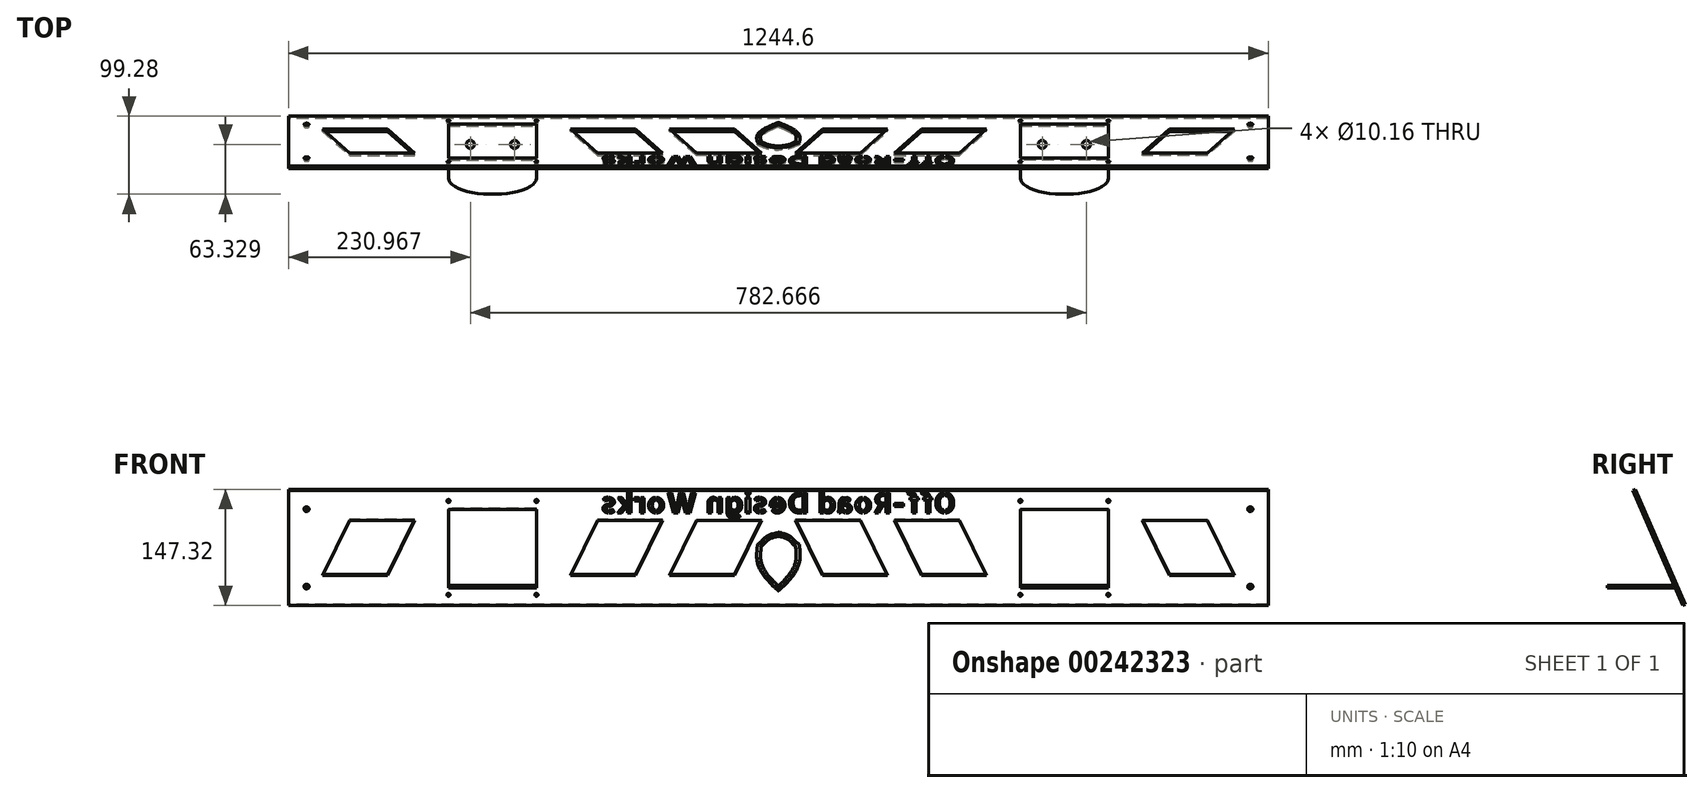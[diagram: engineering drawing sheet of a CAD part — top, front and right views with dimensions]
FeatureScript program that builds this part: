
annotation { "Feature Type Name" : "Feature", "Feature Type Description" : "" }
export const myFeature = defineFeature(function(context is Context, id is Id, definition is map)
    precondition{}
    {
        {
            var Q0;
            Q0=qCreatedBy(makeId("Right.planeOp"),FACE);
            var sketch = newSketch(context, id + "F0", { "sketchPlane" : qUnion([Q0])});
            skLineSegment(sketch, "E0", {"start": v(0, 0) * mm, "end": v(-63.5, 146.05) * mm});
            skLineSegment(sketch, "E1", {"start": v(-63.5, 146.05) * mm, "end": v(-66.41, 144.78) * mm});
            skLineSegment(sketch, "E2", {"start": v(-66.41, 144.78) * mm, "end": v(-2.91, -1.27) * mm});
            skLineSegment(sketch, "E3", {"start": v(-2.91, -1.27) * mm, "end": v(0, 0) * mm});
            skSolve(sketch);
        }
        {
            var Q0;
            Q0 = qSketchRegion(id + "F0", true);
            extrude(context, id + "F1", {"entities" : qUnion([Q0]), "depth" : 622.3 * mm, "hasSecondDirection" : true, "secondDirectionOppositeDirection" : true, "secondDirectionDepth" : 622.3 * mm});
        }
        {
            var Q0;
            Q0=makeQuery(id+"F1.opExtrude","SWEPT_FACE",FACE,{"disambiguationData":[OSD([sQuery(id+"F0.wireOp",EDGE,"E0")])]});
            var sketch = newSketch(context, id + "F2", { "sketchPlane" : qUnion([Q0])});
            skSolve(sketch);
        }
        {
            var Q0;
            {var subQ0=sQuery(id+"F0.wireOp",EDGE,"E0");Q0=makeQuery(id+"F2.imprint","IMPRINT",FACE,{"disambiguationData":[TD([[makeQuery(id+"F2.imprint","IMPRINT",EDGE,{"derivedFrom":makeQuery(id+"F1.opExtrude","CAP_EDGE",EDGE,{"disambiguationData":[OSD([subQ0])],"isStart":true})}),1.0]])]});}
            var sketch = newSketch(context, id + "F3", { "sketchPlane" : qUnion([Q0])});
            skLineSegment(sketch, "E4", {"start": v(0, 0) * mm, "end": v(0, -192.6) * mm, "construction": true});
            skLineSegment(sketch, "E5", {"start": v(-307.34, 133.22) * mm, "end": v(-419.1, 133.22) * mm});
            skLineSegment(sketch, "E6", {"start": v(-419.1, 133.22) * mm, "end": v(-419.1, 26.03) * mm});
            skLineSegment(sketch, "E7", {"start": v(-419.1, 26.03) * mm, "end": v(-307.34, 26.03) * mm});
            skLineSegment(sketch, "E8", {"start": v(-307.34, 26.03) * mm, "end": v(-307.34, 133.22) * mm});
            skLineSegment(sketch, "E9", {"start": v(-462.28, 117.73) * mm, "end": v(-544.83, 117.73) * mm});
            skLineSegment(sketch, "E10", {"start": v(-544.83, 117.73) * mm, "end": v(-579.12, 41.53) * mm});
            skLineSegment(sketch, "E11", {"start": v(-579.12, 41.53) * mm, "end": v(-496.57, 41.53) * mm});
            skLineSegment(sketch, "E12", {"start": v(-496.57, 41.53) * mm, "end": v(-462.28, 117.73) * mm});
            skLineSegment(sketch, "E13", {"start": v(-229.87, 117.73) * mm, "end": v(-147.32, 117.73) * mm});
            skLineSegment(sketch, "E14", {"start": v(-147.32, 117.73) * mm, "end": v(-181.6, 41.53) * mm});
            skLineSegment(sketch, "E15", {"start": v(-181.6, 41.53) * mm, "end": v(-264.16, 41.53) * mm});
            skLineSegment(sketch, "E16", {"start": v(-264.16, 41.53) * mm, "end": v(-229.87, 117.73) * mm});
            skLineSegment(sketch, "E17.1.0.0", {"start": v(-21.59, 117.73) * mm, "end": v(-55.88, 41.53) * mm});
            skLineSegment(sketch, "E17.1.0.1", {"start": v(-55.88, 41.53) * mm, "end": v(-138.43, 41.53) * mm});
            skLineSegment(sketch, "E17.1.0.2", {"start": v(-138.43, 41.53) * mm, "end": v(-104.14, 117.73) * mm});
            skLineSegment(sketch, "E17.1.0.3", {"start": v(-104.14, 117.73) * mm, "end": v(-21.59, 117.73) * mm});
            skLineSegment(sketch, "E17.direction1", {"start": v(-229.87, 117.73) * mm, "end": v(-104.14, 117.73) * mm, "construction": true});
            skLineSegment(sketch, "E18.MirrorCS", {"start": v(104.14, 117.73) * mm, "end": v(21.59, 117.73) * mm});
            skLineSegment(sketch, "E19.MirrorCS", {"start": v(138.43, 41.53) * mm, "end": v(104.14, 117.73) * mm});
            skLineSegment(sketch, "E20.MirrorCS", {"start": v(21.59, 117.73) * mm, "end": v(55.88, 41.53) * mm});
            skLineSegment(sketch, "E21.MirrorCS", {"start": v(55.88, 41.53) * mm, "end": v(138.43, 41.53) * mm});
            skLineSegment(sketch, "E22.MirrorCS", {"start": v(147.32, 117.73) * mm, "end": v(181.6, 41.53) * mm});
            skLineSegment(sketch, "E23.MirrorCS", {"start": v(264.16, 41.53) * mm, "end": v(229.87, 117.73) * mm});
            skLineSegment(sketch, "E24.MirrorCS", {"start": v(229.87, 117.73) * mm, "end": v(104.14, 117.73) * mm, "construction": true});
            skLineSegment(sketch, "E25.MirrorCS", {"start": v(181.6, 41.53) * mm, "end": v(264.16, 41.53) * mm});
            skLineSegment(sketch, "E26.MirrorCS", {"start": v(419.1, 26.03) * mm, "end": v(307.34, 26.03) * mm});
            skLineSegment(sketch, "E27.MirrorCS", {"start": v(419.1, 133.22) * mm, "end": v(419.1, 26.03) * mm});
            skLineSegment(sketch, "E28.MirrorCS", {"start": v(307.34, 26.03) * mm, "end": v(307.34, 133.22) * mm});
            skLineSegment(sketch, "E29.MirrorCS", {"start": v(307.34, 133.22) * mm, "end": v(419.1, 133.22) * mm});
            skLineSegment(sketch, "E30.MirrorCS", {"start": v(496.57, 41.53) * mm, "end": v(462.28, 117.73) * mm});
            skLineSegment(sketch, "E31.MirrorCS", {"start": v(462.28, 117.73) * mm, "end": v(544.83, 117.73) * mm});
            skLineSegment(sketch, "E32.MirrorCS", {"start": v(544.83, 117.73) * mm, "end": v(579.12, 41.53) * mm});
            skLineSegment(sketch, "E33.MirrorCS", {"start": v(579.12, 41.53) * mm, "end": v(496.57, 41.53) * mm});
            skLineSegment(sketch, "E34", {"start": v(147.32, 117.73) * mm, "end": v(229.87, 117.73) * mm});
            skSolve(sketch);
        }
        {
            var Q0;
            Q0 = qSketchRegion(id + "F3", true);
            var Q1;
            Q1=makeQuery(id+"F1.opExtrude","SWEPT_FACE",FACE,{"disambiguationData":[OSD([sQuery(id+"F0.wireOp",EDGE,"E2")])]});
            extrude(context, id + "F4", {"entities" : qUnion([Q0]), "operationType" : NewBodyOperationType.REMOVE, "endBound" : BoundingType.UP_TO_SURFACE, "oppositeDirection" : true, "endBoundEntityFace" : qUnion([Q1]), "depth" : 25.4 * mm});
        }
        {
            var Q0;
            {var subQ0=sQuery(id+"F0.wireOp",EDGE,"E0");Q0=makeQuery(id+"F2.imprint","IMPRINT",FACE,{"disambiguationData":[TD([[makeQuery(id+"F2.imprint","IMPRINT",EDGE,{"derivedFrom":makeQuery(id+"F1.opExtrude","CAP_EDGE",EDGE,{"disambiguationData":[OSD([subQ0])],"isStart":true})}),1.0]])]});}
            var sketch = newSketch(context, id + "F5", { "sketchPlane" : qUnion([Q0])});
            skCircle(sketch, "E35", {"center": v(-419.1, 144.65) * mm, "radius": 1.9 * mm});
            skCircle(sketch, "E36", {"center": v(-307.34, 144.65) * mm, "radius": 1.9 * mm});
            skCircle(sketch, "E37", {"center": v(-419.1, 14.6) * mm, "radius": 1.9 * mm});
            skCircle(sketch, "E38", {"center": v(-307.34, 14.6) * mm, "radius": 1.9 * mm});
            skLineSegment(sketch, "E39", {"start": v(0, 0) * mm, "end": v(0, -78.26) * mm, "construction": true});
            skCircle(sketch, "E40.MirrorC", {"center": v(307.34, 144.65) * mm, "radius": 1.9 * mm});
            skCircle(sketch, "E41.MirrorC", {"center": v(419.1, 144.65) * mm, "radius": 1.9 * mm});
            skCircle(sketch, "E42.MirrorC", {"center": v(419.1, 14.6) * mm, "radius": 1.9 * mm});
            skCircle(sketch, "E43.MirrorC", {"center": v(307.34, 14.6) * mm, "radius": 1.9 * mm});
            skCircle(sketch, "E44", {"center": v(-599.44, 133.22) * mm, "radius": 3.18 * mm});
            skCircle(sketch, "E45", {"center": v(-599.44, 26.03) * mm, "radius": 3.18 * mm});
            skCircle(sketch, "E46.MirrorC", {"center": v(599.44, 26.03) * mm, "radius": 3.18 * mm});
            skCircle(sketch, "E47.MirrorC", {"center": v(599.44, 133.22) * mm, "radius": 3.18 * mm});
            skSolve(sketch);
        }
        {
            var Q0;
            Q0 = qSketchRegion(id + "F5", true);
            var Q1;
            Q1=makeQuery(id+"F1.opExtrude","SWEPT_FACE",FACE,{"disambiguationData":[OSD([sQuery(id+"F0.wireOp",EDGE,"E2")])]});
            extrude(context, id + "F6", {"entities" : qUnion([Q0]), "operationType" : NewBodyOperationType.REMOVE, "endBound" : BoundingType.UP_TO_SURFACE, "oppositeDirection" : true, "endBoundEntityFace" : qUnion([Q1]), "depth" : 25.4 * mm});
        }
        {
            var Q0;
            {var subQ0=sQuery(id+"F0.wireOp",EDGE,"E0");Q0=makeQuery(id+"F2.imprint","IMPRINT",FACE,{"disambiguationData":[TD([[makeQuery(id+"F2.imprint","IMPRINT",EDGE,{"derivedFrom":makeQuery(id+"F1.opExtrude","CAP_EDGE",EDGE,{"disambiguationData":[OSD([subQ0])],"isStart":true})}),1.0]])]});}
            var sketch = newSketch(context, id + "F7", { "sketchPlane" : qUnion([Q0])});
            skText(sketch, "E48", { "text": "Off-Road Design Works", "fontName": "AllertaStencil-Regular.ttf"});
            skLineSegment(sketch, "E49", {"start": v(0, 128.23) * mm, "end": v(0, 0) * mm, "construction": true});
            const initialGuessF7  = {"E48": [-0.22543, 0.12823, 1, 0, 0.02722]};
            skSetInitialGuess(sketch, initialGuessF7);
            skSolve(sketch);
        }
        {
            var Q0;
            Q0 = qSketchRegion(id + "F7", true);
            var Q1;
            Q1=makeQuery(id+"F1.opExtrude","SWEPT_FACE",FACE,{"disambiguationData":[OSD([sQuery(id+"F0.wireOp",EDGE,"E2")])]});
            extrude(context, id + "F8", {"entities" : qUnion([Q0]), "operationType" : NewBodyOperationType.REMOVE, "endBound" : BoundingType.UP_TO_SURFACE, "oppositeDirection" : true, "endBoundEntityFace" : qUnion([Q1]), "depth" : 25.4 * mm});
        }
        {
            var Q0;
            Q0=qCreatedBy(makeId("Top.planeOp"),FACE);
            var Q1;
            Q1=makeQuery(id+"F4.boolean.opBoolean","COPY",VERTEX,{"derivedFrom":makeQuery(id+"F4.opExtrude","CAP_VERTEX",VERTEX,{"disambiguationData":[OSD([sQuery(id+"F3.wireOp",EDGE,"E7"),sQuery(id+"F3.wireOp",EDGE,"E8")])],"isStart":true})});
            cPlane(context, id + "F9", {"entities" : qUnion([Q0, Q1]), "cplaneType" : CPlaneType.PLANE_POINT, "offset" : 25.4 * mm, "width" : 152.4 * mm, "height" : 152.4 * mm});
        }
        {
            var Q0;
            Q0=qCreatedBy(id+"F9.planeOp",FACE);
            var sketch = newSketch(context, id + "F10", { "sketchPlane" : qUnion([Q0])});
            skLineSegment(sketch, "E50", {"start": v(419.1, -10.38) * mm, "end": v(419.1, -78.96) * mm});
            skLineSegment(sketch, "E51", {"start": v(307.34, -10.38) * mm, "end": v(307.34, -78.96) * mm});
            skLineSegment(sketch, "E52", {"start": v(363.22, -11.11) * mm, "end": v(363.22, -61.05) * mm, "construction": true});
            skEllipticalArc(sketch, "E53", {});
            skLineSegment(sketch, "E54", {"start": v(307.34, -10.38) * mm, "end": v(419.1, -10.38) * mm});
            skLineSegment(sketch, "E55", {"start": v(0, 0) * mm, "end": v(0, -97.93) * mm, "construction": true});
            skLineSegment(sketch, "E56.MirrorCS", {"start": v(-307.34, -10.38) * mm, "end": v(-307.34, -78.96) * mm});
            skLineSegment(sketch, "E57.MirrorCS", {"start": v(-307.34, -10.38) * mm, "end": v(-419.1, -10.38) * mm});
            skLineSegment(sketch, "E58.MirrorCS", {"start": v(-419.1, -10.38) * mm, "end": v(-419.1, -78.96) * mm});
            skEllipticalArc(sketch, "E59.MirrorCS", {});
            skCircle(sketch, "E60", {"center": v(391.33, -35.95) * mm, "radius": 5.08 * mm});
            skCircle(sketch, "E61.MirrorC", {"center": v(335.1, -35.95) * mm, "radius": 5.08 * mm});
            skCircle(sketch, "E62.MirrorC", {"center": v(-335.1, -35.95) * mm, "radius": 5.08 * mm});
            skCircle(sketch, "E63.MirrorC", {"center": v(-391.33, -35.95) * mm, "radius": 5.08 * mm});
            const initialGuessF10  = {"E53": [0.36322, -0.07896051125903271, 1, 0, 0.05588, 0.02032, 3.141592653589793, 0], "E59.MirrorCS": [-0.36322, -0.07896051125903271, -1, 0, 0.05588, 0.02032, 0, 3.141592653589793]};
            skSetInitialGuess(sketch, initialGuessF10);
            skSolve(sketch);
        }
        {
            var Q0;
            Q0 = qSketchRegion(id + "F10", true);
            extrude(context, id + "F11", {"entities" : qUnion([Q0]), "operationType" : NewBodyOperationType.ADD, "oppositeDirection" : true, "depth" : 3.17 * mm});
        }
        {
            var Q0;
            {var subQ0=sQuery(id+"F0.wireOp",EDGE,"E0");Q0=makeQuery(id+"F2.imprint","IMPRINT",FACE,{"disambiguationData":[TD([[makeQuery(id+"F2.imprint","IMPRINT",EDGE,{"derivedFrom":makeQuery(id+"F1.opExtrude","CAP_EDGE",EDGE,{"disambiguationData":[OSD([subQ0])],"isStart":true})}),1.0]])]});}
            var sketch = newSketch(context, id + "F12", { "sketchPlane" : qUnion([Q0])});
            skLineSegment(sketch, "E64", {"start": v(0, 0) * mm, "end": v(0, 201.67) * mm, "construction": true});
            skFitSpline(sketch, "E65", {"points": [v(0, 20.03) * mm, v(-26.56, 84.7) * mm], "startDerivative": vector(-94.3, 90.63) * mm, "endDerivative": vector(5.61, 60.71) * mm});
            skFitSpline(sketch, "E66", {"points": [v(-26.56, 84.7) * mm, v(0, 100.83) * mm], "startDerivative": vector(26.56, 16.14) * mm, "endDerivative": vector(61.74, 11.54) * mm});
            skFitSpline(sketch, "E67.MirrorCS", {"points": [v(0, 20.03) * mm, v(26.56, 84.7) * mm], "startDerivative": vector(94.3, 90.63) * mm, "endDerivative": vector(-5.61, 60.71) * mm});
            skFitSpline(sketch, "E68.MirrorCS", {"points": [v(26.56, 84.7) * mm, v(0, 100.83) * mm], "startDerivative": vector(-26.56, 16.14) * mm, "endDerivative": vector(-61.74, 11.54) * mm});
            skFitSpline(sketch, "E69.0", {"points": [v(23.92, 80.35) * mm, v(23.24, 80.77) * mm, v(21.97, 81.62) * mm, v(20.33, 82.96) * mm, v(18.93, 84.3) * mm, v(17.74, 85.6) * mm, v(16.72, 86.8) * mm, v(15.81, 87.88) * mm, v(14.97, 88.84) * mm, v(14.14, 89.7) * mm, v(13.26, 90.5) * mm, v(12.26, 91.28) * mm, v(11.04, 92.05) * mm, v(9.02, 93.1) * mm, v(5.57, 94.4) * mm, v(1.5, 95.39) * mm, v(-0.93, 95.84) * mm]});
            skFitSpline(sketch, "E69.1", {"points": [v(-3.52, 23.7) * mm, v(0.32, 27.38) * mm, v(6.9, 34.24) * mm, v(13.91, 43.13) * mm, v(18.48, 50.85) * mm, v(21.14, 57.64) * mm, v(22.39, 63.92) * mm, v(22.65, 70.18) * mm, v(22.24, 76.81) * mm, v(21.74, 81.66) * mm, v(21.5, 84.22) * mm]});
            skFitSpline(sketch, "E69.2", {"points": [v(3.52, 23.7) * mm, v(-0.32, 27.38) * mm, v(-6.9, 34.24) * mm, v(-13.91, 43.13) * mm, v(-18.48, 50.85) * mm, v(-21.14, 57.64) * mm, v(-22.39, 63.92) * mm, v(-22.65, 70.18) * mm, v(-22.24, 76.81) * mm, v(-21.74, 81.66) * mm, v(-21.5, 84.22) * mm]});
            skFitSpline(sketch, "E69.3", {"points": [v(-23.92, 80.35) * mm, v(-23.24, 80.77) * mm, v(-21.97, 81.62) * mm, v(-20.33, 82.96) * mm, v(-18.93, 84.3) * mm, v(-17.74, 85.6) * mm, v(-16.72, 86.8) * mm, v(-15.81, 87.88) * mm, v(-14.97, 88.84) * mm, v(-14.14, 89.7) * mm, v(-13.26, 90.5) * mm, v(-12.26, 91.28) * mm, v(-11.04, 92.05) * mm, v(-9.02, 93.1) * mm, v(-5.57, 94.4) * mm, v(-1.5, 95.39) * mm, v(0.93, 95.84) * mm]});
            skLineSegment(sketch, "E70", {"start": v(4.83, 99.77) * mm, "end": v(4.83, 94.5) * mm});
            skLineSegment(sketch, "E71.MirrorCS", {"start": v(-4.83, 99.77) * mm, "end": v(-4.83, 94.5) * mm});
            skLineSegment(sketch, "E72.trimOffspring", {"start": v(4.83, 32.22) * mm, "end": v(4.83, 24.82) * mm});
            skLineSegment(sketch, "E73.trimOffspring", {"start": v(-4.83, 32.22) * mm, "end": v(-4.83, 24.82) * mm});
            skText(sketch, "E74", { "text": "OD", "fontName": "AllertaStencil-Regular.ttf"});
            skText(sketch, "E75", { "text": "W", "fontName": "AllertaStencil-Regular.ttf"});
            const initialGuessF12  = {"E74": [-0.01742, 0.06557, 1, 0, 0.01682], "E75": [-0.01143, 0.04464, 1, 0, 0.01545]};
            skSetInitialGuess(sketch, initialGuessF12);
            skSolve(sketch);
        }
        {
            var Q0;
            Q0 = qSketchRegion(id + "F12", true);
            var Q1;
            Q1=makeQuery(id+"F1.opExtrude","SWEPT_FACE",FACE,{"disambiguationData":[OSD([sQuery(id+"F0.wireOp",EDGE,"E2")])]});
            extrude(context, id + "F13", {"entities" : qUnion([Q0]), "operationType" : NewBodyOperationType.REMOVE, "endBound" : BoundingType.UP_TO_SURFACE, "oppositeDirection" : true, "endBoundEntityFace" : qUnion([Q1]), "depth" : 25.4 * mm});
        }
    });
